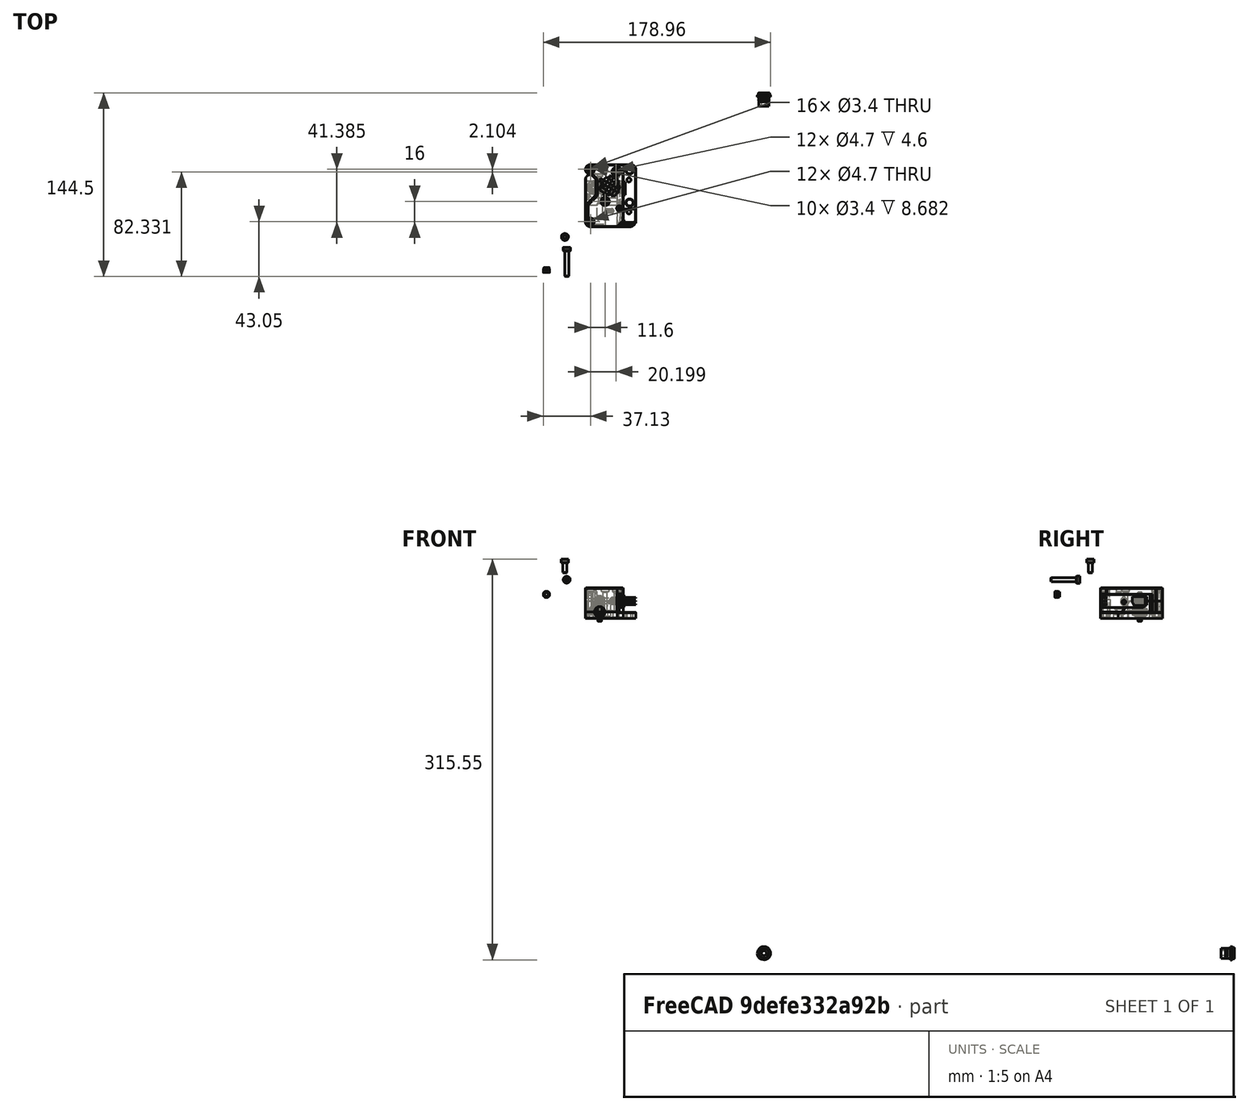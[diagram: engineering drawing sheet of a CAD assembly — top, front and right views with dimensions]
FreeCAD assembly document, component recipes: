
FREECAD ASSEMBLY — COMPONENT RECIPES ("ERCF_sensor_faceRemoved_safetysave")

This assembly document has 3 components, labeled P0..P2 below (a component is one placed body or linked part). 1 of them carries a construction recipe — the FreeCAD feature program that regenerates the part from scratch, quoted from this document or its linked companion documents; the rest are supplied as boundary geometry only. No exploded tour is included for this assembly.
COMPONENT P0 — recipe-attached ("Body", modeled in this document).
Construction recipe (the document's own serialized feature program — sketch geometry with constraints, then the solid features built on it; lengths are millimeters unless a unit is written):

FEATURE [Part::SubShapeBinder] Import  label="Import(COMPOUND.1)"
  BindCopyOnChange = 0
  BindMode = 0
  ClaimChildren = false
  Context = -> Body [Import.]
  EdgeTolerance = 1e-06
  FillStyle = 0
  Fuse = false
  InvalidShape = false
  MakeFace = false
  MergeEdges = true
  OffsetFill = false
  OffsetIntersection = false
  OffsetJoinType = 0
  OffsetOpenResult = false
  Outline = false
  PartialLoad = false
  Relative = true
  SplitEdges = false
  Support = -> [Compound002_child1]
  TightBound = false
  TreeRank = 311
  ValidateShape = false
  _Version = 8
FEATURE [Sketcher::SketchObject] Sketch
  ArcFitTolerance = 1e-06
  AttachmentSupport = -> [Import]
  ExternalBSplineMaxDegree = 5
  ExternalBSplineTolerance = 0.0001
  ExternalGeometry = -> [Import]
  FullyConstrained = true
  InternalTolerance = 1e-06
  InvalidShape = false
  MakeInternals = false
  MapMode = 5
  Placement = pos=(13.95,-8e-16,0) rot=(0.57735,0.57735,0.57735;2.0944rad)
  Support = -> [Import]
  TreeRank = 312
  ValidateShape = false
  sketch-geometry (4):
    g0: LineSegment StartX=-31 StartY=15.8 StartZ=0 EndX=-15.3 EndY=15.8 EndZ=0
    g1: LineSegment StartX=-15.3 StartY=15.8 StartZ=0 EndX=-15.3 EndY=1.8 EndZ=0
    g2: LineSegment StartX=-15.3 StartY=1.8 StartZ=0 EndX=-31 EndY=1.8 EndZ=0
    g3: LineSegment StartX=-31 StartY=1.8 StartZ=0 EndX=-31 EndY=15.8 EndZ=0
  constraints (12):
    c: Coincident(g0,g1)
    c: Coincident(g1,g2)
    c: Coincident(g2,g3)
    c: Coincident(g3,g0)
    c: Horizontal(g0)
    c: Horizontal(g2)
    c: Vertical(g1)
    c: Vertical(g3)
    c: DistanceX(g0,g0) = 15.7
    c: DistanceY(g1,g1) = 14
    c: DistanceX(g1,g-1) = 15.3
    c: DistanceY(g-1,g1) = 1.8
FEATURE [PartDesign::Pad] Pad
  AddSubType = 0
  AlongSketchNormal = false
  AutoTaperInnerAngle = true
  CheckUpToFaceLimits = true
  ClaimChildren = false
  Direction = (1,0,0)
  Fit = 0
  FitJoin = 0
  InnerFit = 0
  InnerFitJoin = 0
  InvalidShape = false
  Length = 10
  Length2 = 10
  Linearize = true
  NewSolid = false
  Profile = -> Sketch
  ReferenceAxis = -> Sketch [N_Axis]
  Reversed = true
  Suppress = false
  TaperInnerAngle = 0
  TaperInnerAngleRev = 0
  TreeRank = 313
  Type = 0
  ValidateShape = false
  _ProfileBasedVersion = 1
FEATURE [Sketcher::SketchObject] Sketch001
  ArcFitTolerance = 1e-06
  AttachmentSupport = -> [Import]
  ExternalBSplineMaxDegree = 5
  ExternalBSplineTolerance = 0.0001
  FullyConstrained = true
  InternalTolerance = 1e-06
  InvalidShape = false
  MakeInternals = false
  MapMode = 5
  Placement = pos=(13.95,-8e-16,0) rot=(0.57735,0.57735,0.57735;2.0944rad)
  Support = -> [Import]
  TreeRank = 314
  ValidateShape = false
  sketch-geometry (4):
    g0: LineSegment StartX=-31 StartY=12 StartZ=0 EndX=-21 EndY=12 EndZ=0
    g1: LineSegment StartX=-21 StartY=12 StartZ=0 EndX=-21 EndY=5.7 EndZ=0
    g2: LineSegment StartX=-21 StartY=5.7 StartZ=0 EndX=-31 EndY=5.7 EndZ=0
    g3: LineSegment StartX=-31 StartY=5.7 StartZ=0 EndX=-31 EndY=12 EndZ=0
  constraints (12):
    c: Coincident(g0,g1)
    c: Coincident(g1,g2)
    c: Coincident(g2,g3)
    c: Coincident(g3,g0)
    c: Horizontal(g0)
    c: Horizontal(g2)
    c: Vertical(g1)
    c: Vertical(g3)
    c: DistanceX(g2,g-1) = 31
    c: DistanceY(g-1,g2) = 5.7
    c: DistanceY(g1,g1) = 6.3
    c: DistanceX(g0,g0) = 10
FEATURE [PartDesign::Pad] Pad001
  AddSubType = 0
  AlongSketchNormal = false
  AutoTaperInnerAngle = true
  BaseFeature = -> Pad
  CheckUpToFaceLimits = true
  ClaimChildren = false
  Direction = (1,0,0)
  Fit = 0
  FitJoin = 0
  InnerFit = 0
  InnerFitJoin = 0
  InvalidShape = false
  Length = 13
  Length2 = 10
  Linearize = true
  NewSolid = false
  Profile = -> Sketch001
  ReferenceAxis = -> Sketch001 [N_Axis]
  Reversed = true
  Suppress = false
  TaperInnerAngle = 0
  TaperInnerAngleRev = 0
  TreeRank = 341
  Type = 0
  ValidateShape = false
  _ProfileBasedVersion = 1
  _Siblings = -> [Pad]
FEATURE [PartDesign::Body] Body
  AutoGroupSolids = true
  ClaimAllChildren = false
  ExportMode = 0
  Group = -> [Import,Sketch,Pad,Sketch001,Pad001]
  InvalidShape = false
  Origin = -> Origin016
  SingleSolid = true
  Tip = -> Pad001
  TreeRank = 320
  ValidateShape = false
  _ExportChildren = -> [Import,Pad001]
  _GroupVersion = 1
COMPONENT P1 — geometry summary ("Part017"; no construction recipe available for this part):
  bounding box: 28.4 x 10.0 x 3.3 mm
  tessellated surface: 1,000 triangles
  volume: 171 mm^3 (18% of its bounding box)
  symmetry: 2-fold rotationally symmetric about the x axis; 2-fold rotationally symmetric about the y axis; 2-fold rotationally symmetric about the z axis; mirror-symmetric across its x mid-plane, y mid-plane, z mid-plane
COMPONENT P2 — geometry summary ("LED_Trhoughhole"; no construction recipe available for this part):
  bounding box: 11.2 x 4.2 x 4.2 mm
  tessellated surface: 1,004 triangles
  volume: 142 mm^3 (72% of its bounding box)
  symmetry: revolution-symmetric about the z axis through its bounding-box center; mirror-symmetric across its x mid-plane, y mid-plane
PROVENANCE & LICENSES
A FreeCAD (.FCStd) document from a public repository crawl; recipes are the document's own serialized feature recipes (and, for linked parts, companion documents' recipes).
License: gpl-3.0.
